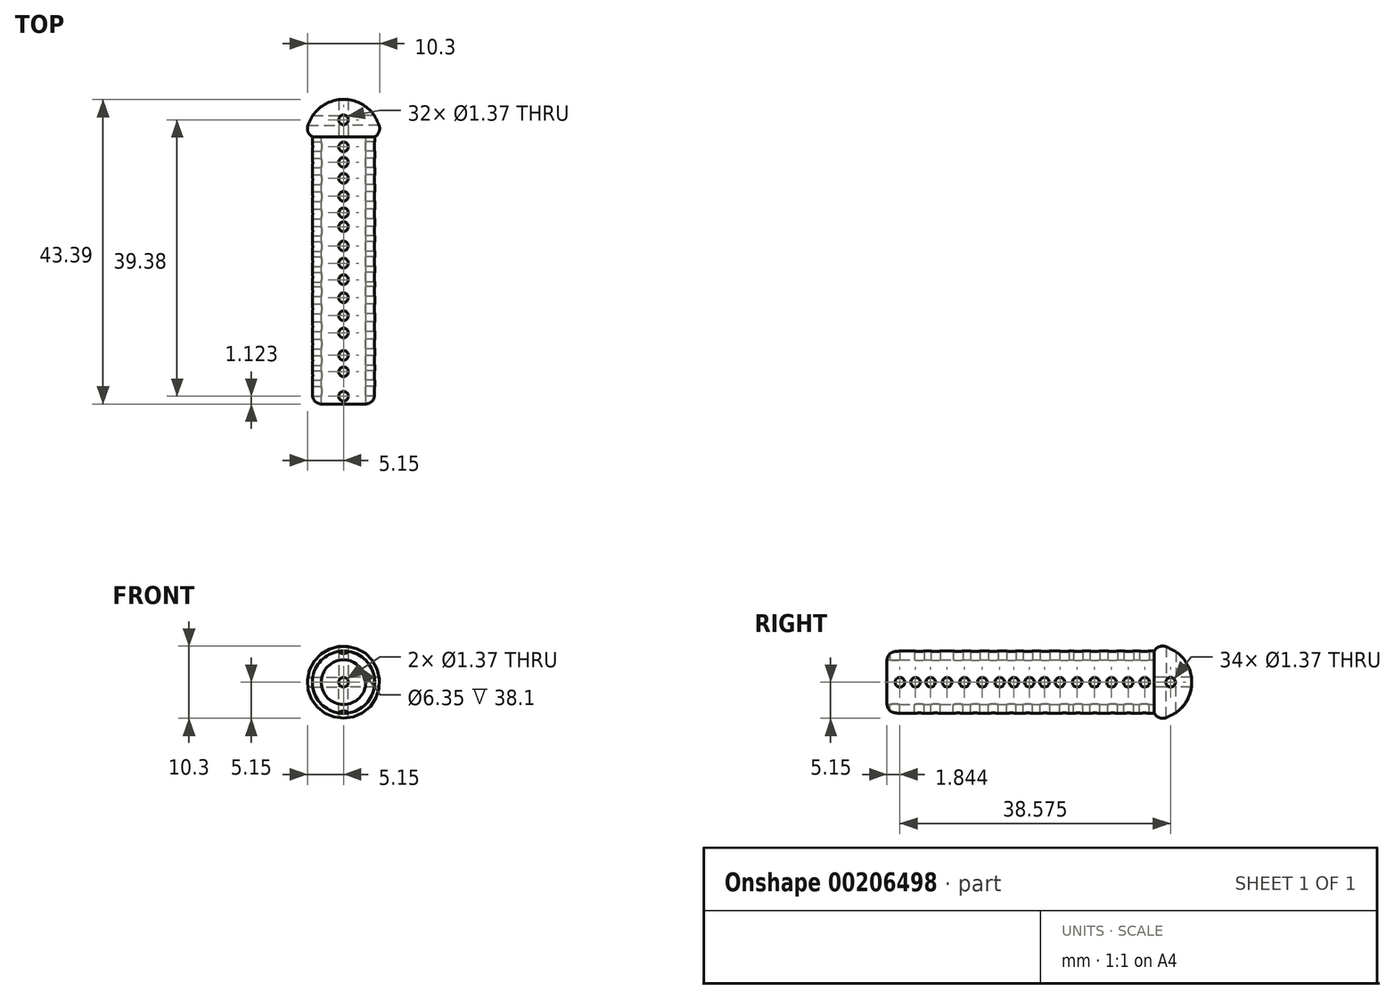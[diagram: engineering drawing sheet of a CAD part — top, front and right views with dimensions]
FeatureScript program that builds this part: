
annotation { "Feature Type Name" : "Feature", "Feature Type Description" : "" }
export const myFeature = defineFeature(function(context is Context, id is Id, definition is map)
    precondition{}
    {
        {
            var Q0;
            Q0=qCreatedBy(makeId("Front.planeOp"),FACE);
            var sketch = newSketch(context, id + "F0", { "sketchPlane" : qUnion([Q0])});
            skCircle(sketch, "E0", {"center": v(0, 0) * mm, "radius": 4.45 * mm});
            skCircle(sketch, "E1", {"center": v(0, 0) * mm, "radius": 3.18 * mm});
            skSolve(sketch);
        }
        {
            var Q0;
            Q0 = qSketchRegion(id + "F0", true);
            extrude(context, id + "F1", {"entities" : qUnion([Q0]), "depth" : 38.1 * mm});
        }
        {
            var Q0;
            Q0=qCreatedBy(makeId("Top.planeOp"),FACE);
            var sketch = newSketch(context, id + "F2", { "sketchPlane" : qUnion([Q0])});
            skArc(sketch, "E2", {"start": v(5.33, 0) * mm, "mid": v(3.77, 3.77) * mm, "end": v(0, 5.33) * mm});
            skLineSegment(sketch, "E3", {"start": v(0, 5.33) * mm, "end": v(0, 0) * mm});
            skLineSegment(sketch, "E4", {"start": v(5.33, 0) * mm, "end": v(0, 0) * mm});
            skSolve(sketch);
        }
        {
            var Q0;
            Q0 = qSketchRegion(id + "F2", true);
            var Q1;
            Q1=sQuery(id+"F2.wireOp",EDGE,"E3");
            revolve(context, id + "F3", {"operationType" : NewBodyOperationType.ADD, "entities" : qUnion([Q0]), "axis" : qUnion([Q1]), "revolveType" : RevolveType.FULL});
        }
        {
            var Q0;
            Q0 = qSketchRegion(id + "F0", true);
            extrude(context, id + "F4", {"entities" : qUnion([Q0]), "operationType" : NewBodyOperationType.ADD, "depth" : 38.1 * mm});
        }
        {
            var Q0;
            Q0=qCreatedBy(makeId("Right.planeOp"),FACE);
            var sketch = newSketch(context, id + "F5", { "sketchPlane" : qUnion([Q0])});
            skCircle(sketch, "E5", {"center": v(-1.37, 0) * mm, "radius": 0.64 * mm});
            skSolve(sketch);
        }
        {
            var Q0;
            Q0=sQuery(id+"F5.wireOp",VERTEX,"E5.center");
            var Q1;
            Q1=makeQuery(id+"F1.opExtrude","SWEPT_BODY",BODY,{"disambiguationData":[OSD([sQuery(id+"F0.wireOp",EDGE,"E0"),sQuery(id+"F0.wireOp",EDGE,"E1")])]});
            hole(context, id + "F6", {"style" : HoleStyle.SIMPLE, "endStyle" : HoleEndStyle.THROUGH, "holeDiameter" : 1.37 * mm, "locations" : qUnion([Q0]), "scope" : qUnion([Q1]), "isTappedThrough" : true});
        }
        {
            var Q0;
            Q0=qCreatedBy(makeId("Right.planeOp"),FACE);
            var sketch = newSketch(context, id + "F7", { "sketchPlane" : qUnion([Q0])});
            skCircle(sketch, "E6", {"center": v(-3.72, 0) * mm, "radius": 0.69 * mm});
            skSolve(sketch);
        }
        {
            var Q0;
            Q0=sQuery(id+"F5.wireOp",VERTEX,"E5.center");
            var Q1;
            Q1=makeQuery(id+"F1.opExtrude","SWEPT_BODY",BODY,{"disambiguationData":[OSD([sQuery(id+"F0.wireOp",EDGE,"E0"),sQuery(id+"F0.wireOp",EDGE,"E1")])]});
            hole(context, id + "F8", {"style" : HoleStyle.SIMPLE, "endStyle" : HoleEndStyle.THROUGH, "oppositeDirection" : true, "holeDiameter" : 1.37 * mm, "locations" : qUnion([Q0]), "scope" : qUnion([Q1]), "isTappedThrough" : true});
        }
        {
            var Q0;
            Q0=qCreatedBy(makeId("Right.planeOp"),FACE);
            var sketch = newSketch(context, id + "F9", { "sketchPlane" : qUnion([Q0])});
            skCircle(sketch, "E7", {"center": v(-6.1, 0) * mm, "radius": 0.69 * mm});
            skSolve(sketch);
        }
        {
            var Q0;
            Q0=sQuery(id+"F9.wireOp",VERTEX,"E7.center");
            var Q1;
            Q1=makeQuery(id+"F1.opExtrude","SWEPT_BODY",BODY,{"disambiguationData":[OSD([sQuery(id+"F0.wireOp",EDGE,"E0"),sQuery(id+"F0.wireOp",EDGE,"E1")])]});
            hole(context, id + "F10", {"style" : HoleStyle.SIMPLE, "endStyle" : HoleEndStyle.THROUGH, "holeDiameter" : 1.37 * mm, "locations" : qUnion([Q0]), "scope" : qUnion([Q1]), "isTappedThrough" : true});
        }
        {
            var Q0;
            Q0=sQuery(id+"F9.wireOp",VERTEX,"E7.center");
            var Q1;
            Q1=makeQuery(id+"F1.opExtrude","SWEPT_BODY",BODY,{"disambiguationData":[OSD([sQuery(id+"F0.wireOp",EDGE,"E0"),sQuery(id+"F0.wireOp",EDGE,"E1")])]});
            hole(context, id + "F11", {"style" : HoleStyle.SIMPLE, "endStyle" : HoleEndStyle.THROUGH, "oppositeDirection" : true, "holeDiameter" : 1.37 * mm, "locations" : qUnion([Q0]), "scope" : qUnion([Q1]), "isTappedThrough" : true});
        }
        {
            var Q0;
            Q0=sQuery(id+"F7.wireOp",VERTEX,"E6.center");
            var Q1;
            Q1=makeQuery(id+"F1.opExtrude","SWEPT_BODY",BODY,{"disambiguationData":[OSD([sQuery(id+"F0.wireOp",EDGE,"E0"),sQuery(id+"F0.wireOp",EDGE,"E1")])]});
            hole(context, id + "F12", {"style" : HoleStyle.SIMPLE, "endStyle" : HoleEndStyle.THROUGH, "holeDiameter" : 1.37 * mm, "locations" : qUnion([Q0]), "scope" : qUnion([Q1]), "isTappedThrough" : true});
        }
        {
            var Q0;
            Q0=sQuery(id+"F7.wireOp",VERTEX,"E6.center");
            var Q1;
            Q1=makeQuery(id+"F1.opExtrude","SWEPT_BODY",BODY,{"disambiguationData":[OSD([sQuery(id+"F0.wireOp",EDGE,"E0"),sQuery(id+"F0.wireOp",EDGE,"E1")])]});
            hole(context, id + "F13", {"style" : HoleStyle.SIMPLE, "endStyle" : HoleEndStyle.THROUGH, "oppositeDirection" : true, "holeDiameter" : 1.37 * mm, "locations" : qUnion([Q0]), "scope" : qUnion([Q1]), "isTappedThrough" : true});
        }
        {
            var Q0;
            Q0=qCreatedBy(makeId("Right.planeOp"),FACE);
            var sketch = newSketch(context, id + "F14", { "sketchPlane" : qUnion([Q0])});
            skCircle(sketch, "E8", {"center": v(-8.52, 0) * mm, "radius": 0.69 * mm});
            skSolve(sketch);
        }
        {
            var Q0;
            Q0=sQuery(id+"F14.wireOp",VERTEX,"E8.center");
            var Q1;
            Q1=makeQuery(id+"F1.opExtrude","SWEPT_BODY",BODY,{"disambiguationData":[OSD([sQuery(id+"F0.wireOp",EDGE,"E0"),sQuery(id+"F0.wireOp",EDGE,"E1")])]});
            hole(context, id + "F15", {"style" : HoleStyle.SIMPLE, "endStyle" : HoleEndStyle.THROUGH, "holeDiameter" : 1.37 * mm, "locations" : qUnion([Q0]), "scope" : qUnion([Q1]), "isTappedThrough" : true});
        }
        {
            var Q0;
            Q0=sQuery(id+"F14.wireOp",VERTEX,"E8.center");
            var Q1;
            Q1=makeQuery(id+"F1.opExtrude","SWEPT_BODY",BODY,{"disambiguationData":[OSD([sQuery(id+"F0.wireOp",EDGE,"E0"),sQuery(id+"F0.wireOp",EDGE,"E1")])]});
            hole(context, id + "F16", {"style" : HoleStyle.SIMPLE, "endStyle" : HoleEndStyle.THROUGH, "oppositeDirection" : true, "holeDiameter" : 1.37 * mm, "locations" : qUnion([Q0]), "scope" : qUnion([Q1]), "isTappedThrough" : true});
        }
        {
            var Q0;
            Q0=qCreatedBy(makeId("Right.planeOp"),FACE);
            var sketch = newSketch(context, id + "F17", { "sketchPlane" : qUnion([Q0])});
            skCircle(sketch, "E9", {"center": v(-11, 0) * mm, "radius": 0.69 * mm});
            skSolve(sketch);
        }
        {
            var Q0;
            Q0=sQuery(id+"F17.wireOp",VERTEX,"E9.center");
            var Q1;
            Q1=makeQuery(id+"F1.opExtrude","SWEPT_BODY",BODY,{"disambiguationData":[OSD([sQuery(id+"F0.wireOp",EDGE,"E0"),sQuery(id+"F0.wireOp",EDGE,"E1")])]});
            hole(context, id + "F18", {"style" : HoleStyle.SIMPLE, "endStyle" : HoleEndStyle.THROUGH, "holeDiameter" : 1.37 * mm, "locations" : qUnion([Q0]), "scope" : qUnion([Q1]), "isTappedThrough" : true});
        }
        {
            var Q0;
            Q0=sQuery(id+"F17.wireOp",VERTEX,"E9.center");
            var Q1;
            Q1=makeQuery(id+"F1.opExtrude","SWEPT_BODY",BODY,{"disambiguationData":[OSD([sQuery(id+"F0.wireOp",EDGE,"E0"),sQuery(id+"F0.wireOp",EDGE,"E1")])]});
            hole(context, id + "F19", {"style" : HoleStyle.SIMPLE, "endStyle" : HoleEndStyle.THROUGH, "oppositeDirection" : true, "holeDiameter" : 1.37 * mm, "locations" : qUnion([Q0]), "scope" : qUnion([Q1]), "isTappedThrough" : true});
        }
        {
            var Q0;
            Q0=qCreatedBy(makeId("Right.planeOp"),FACE);
            var sketch = newSketch(context, id + "F20", { "sketchPlane" : qUnion([Q0])});
            skCircle(sketch, "E10", {"center": v(-13.45, 0) * mm, "radius": 0.68 * mm});
            skSolve(sketch);
        }
        {
            var Q0;
            Q0=sQuery(id+"F20.wireOp",VERTEX,"E10.center");
            var Q1;
            Q1=makeQuery(id+"F1.opExtrude","SWEPT_BODY",BODY,{"disambiguationData":[OSD([sQuery(id+"F0.wireOp",EDGE,"E0"),sQuery(id+"F0.wireOp",EDGE,"E1")])]});
            hole(context, id + "F21", {"style" : HoleStyle.SIMPLE, "endStyle" : HoleEndStyle.THROUGH, "holeDiameter" : 1.37 * mm, "locations" : qUnion([Q0]), "scope" : qUnion([Q1]), "isTappedThrough" : true});
        }
        {
            var Q0;
            Q0=sQuery(id+"F20.wireOp",VERTEX,"E10.center");
            var Q1;
            Q1=makeQuery(id+"F1.opExtrude","SWEPT_BODY",BODY,{"disambiguationData":[OSD([sQuery(id+"F0.wireOp",EDGE,"E0"),sQuery(id+"F0.wireOp",EDGE,"E1")])]});
            hole(context, id + "F22", {"style" : HoleStyle.SIMPLE, "endStyle" : HoleEndStyle.THROUGH, "oppositeDirection" : true, "holeDiameter" : 1.37 * mm, "locations" : qUnion([Q0]), "scope" : qUnion([Q1]), "isTappedThrough" : true});
        }
        {
            var Q0;
            Q0=qCreatedBy(makeId("Right.planeOp"),FACE);
            var sketch = newSketch(context, id + "F23", { "sketchPlane" : qUnion([Q0])});
            skCircle(sketch, "E11", {"center": v(-15.65, 0) * mm, "radius": 0.69 * mm});
            skSolve(sketch);
        }
        {
            var Q0;
            Q0=sQuery(id+"F23.wireOp",VERTEX,"E11.center");
            var Q1;
            Q1=makeQuery(id+"F1.opExtrude","SWEPT_BODY",BODY,{"disambiguationData":[OSD([sQuery(id+"F0.wireOp",EDGE,"E0"),sQuery(id+"F0.wireOp",EDGE,"E1")])]});
            hole(context, id + "F24", {"style" : HoleStyle.SIMPLE, "endStyle" : HoleEndStyle.THROUGH, "holeDiameter" : 1.37 * mm, "locations" : qUnion([Q0]), "scope" : qUnion([Q1]), "isTappedThrough" : true});
        }
        {
            var Q0;
            Q0=sQuery(id+"F23.wireOp",VERTEX,"E11.center");
            var Q1;
            Q1=makeQuery(id+"F1.opExtrude","SWEPT_BODY",BODY,{"disambiguationData":[OSD([sQuery(id+"F0.wireOp",EDGE,"E0"),sQuery(id+"F0.wireOp",EDGE,"E1")])]});
            hole(context, id + "F25", {"style" : HoleStyle.SIMPLE, "endStyle" : HoleEndStyle.THROUGH, "oppositeDirection" : true, "holeDiameter" : 1.37 * mm, "locations" : qUnion([Q0]), "scope" : qUnion([Q1]), "isTappedThrough" : true});
        }
        {
            var Q0;
            Q0=qCreatedBy(makeId("Right.planeOp"),FACE);
            var sketch = newSketch(context, id + "F26", { "sketchPlane" : qUnion([Q0])});
            skCircle(sketch, "E12", {"center": v(-17.8, 0) * mm, "radius": 0.69 * mm});
            skSolve(sketch);
        }
        {
            var Q0;
            Q0=sQuery(id+"F26.wireOp",VERTEX,"E12.center");
            var Q1;
            Q1=makeQuery(id+"F1.opExtrude","SWEPT_BODY",BODY,{"disambiguationData":[OSD([sQuery(id+"F0.wireOp",EDGE,"E0"),sQuery(id+"F0.wireOp",EDGE,"E1")])]});
            hole(context, id + "F27", {"style" : HoleStyle.SIMPLE, "endStyle" : HoleEndStyle.THROUGH, "holeDiameter" : 1.37 * mm, "locations" : qUnion([Q0]), "scope" : qUnion([Q1]), "isTappedThrough" : true});
        }
        {
            var Q0;
            Q0=sQuery(id+"F26.wireOp",VERTEX,"E12.center");
            var Q1;
            Q1=makeQuery(id+"F1.opExtrude","SWEPT_BODY",BODY,{"disambiguationData":[OSD([sQuery(id+"F0.wireOp",EDGE,"E0"),sQuery(id+"F0.wireOp",EDGE,"E1")])]});
            hole(context, id + "F28", {"style" : HoleStyle.SIMPLE, "endStyle" : HoleEndStyle.THROUGH, "oppositeDirection" : true, "holeDiameter" : 1.37 * mm, "locations" : qUnion([Q0]), "scope" : qUnion([Q1]), "isTappedThrough" : true});
        }
        {
            var Q0;
            Q0=qCreatedBy(makeId("Right.planeOp"),FACE);
            var sketch = newSketch(context, id + "F29", { "sketchPlane" : qUnion([Q0])});
            skCircle(sketch, "E13", {"center": v(-20, 0) * mm, "radius": 0.69 * mm});
            skSolve(sketch);
        }
        {
            var Q0;
            Q0=sQuery(id+"F29.wireOp",VERTEX,"E13.center");
            var Q1;
            Q1=makeQuery(id+"F1.opExtrude","SWEPT_BODY",BODY,{"disambiguationData":[OSD([sQuery(id+"F0.wireOp",EDGE,"E0"),sQuery(id+"F0.wireOp",EDGE,"E1")])]});
            hole(context, id + "F30", {"style" : HoleStyle.SIMPLE, "endStyle" : HoleEndStyle.THROUGH, "holeDiameter" : 1.37 * mm, "locations" : qUnion([Q0]), "scope" : qUnion([Q1]), "isTappedThrough" : true});
        }
        {
            var Q0;
            Q0=sQuery(id+"F29.wireOp",VERTEX,"E13.center");
            var Q1;
            Q1=makeQuery(id+"F1.opExtrude","SWEPT_BODY",BODY,{"disambiguationData":[OSD([sQuery(id+"F0.wireOp",EDGE,"E0"),sQuery(id+"F0.wireOp",EDGE,"E1")])]});
            hole(context, id + "F31", {"style" : HoleStyle.SIMPLE, "endStyle" : HoleEndStyle.THROUGH, "oppositeDirection" : true, "holeDiameter" : 1.37 * mm, "locations" : qUnion([Q0]), "scope" : qUnion([Q1]), "isTappedThrough" : true});
        }
        {
            var Q0;
            Q0=qCreatedBy(makeId("Right.planeOp"),FACE);
            var sketch = newSketch(context, id + "F32", { "sketchPlane" : qUnion([Q0])});
            skCircle(sketch, "E14", {"center": v(-22.04, 0) * mm, "radius": 0.65 * mm});
            skSolve(sketch);
        }
        {
            var Q0;
            Q0=sQuery(id+"F32.wireOp",VERTEX,"E14.center");
            var Q1;
            Q1=makeQuery(id+"F1.opExtrude","SWEPT_BODY",BODY,{"disambiguationData":[OSD([sQuery(id+"F0.wireOp",EDGE,"E0"),sQuery(id+"F0.wireOp",EDGE,"E1")])]});
            hole(context, id + "F33", {"style" : HoleStyle.SIMPLE, "endStyle" : HoleEndStyle.THROUGH, "holeDiameter" : 1.37 * mm, "locations" : qUnion([Q0]), "scope" : qUnion([Q1]), "isTappedThrough" : true});
        }
        {
            var Q0;
            Q0=sQuery(id+"F32.wireOp",VERTEX,"E14.center");
            var Q1;
            Q1=makeQuery(id+"F1.opExtrude","SWEPT_BODY",BODY,{"disambiguationData":[OSD([sQuery(id+"F0.wireOp",EDGE,"E0"),sQuery(id+"F0.wireOp",EDGE,"E1")])]});
            hole(context, id + "F34", {"style" : HoleStyle.SIMPLE, "endStyle" : HoleEndStyle.THROUGH, "oppositeDirection" : true, "holeDiameter" : 1.37 * mm, "locations" : qUnion([Q0]), "scope" : qUnion([Q1]), "isTappedThrough" : true});
        }
        {
            var Q0;
            Q0=qCreatedBy(makeId("Right.planeOp"),FACE);
            var sketch = newSketch(context, id + "F35", { "sketchPlane" : qUnion([Q0])});
            skCircle(sketch, "E15", {"center": v(-24.51, 0) * mm, "radius": 0.7 * mm});
            skSolve(sketch);
        }
        {
            var Q0;
            Q0=sQuery(id+"F35.wireOp",VERTEX,"E15.center");
            var Q1;
            Q1=makeQuery(id+"F1.opExtrude","SWEPT_BODY",BODY,{"disambiguationData":[OSD([sQuery(id+"F0.wireOp",EDGE,"E0"),sQuery(id+"F0.wireOp",EDGE,"E1")])]});
            hole(context, id + "F36", {"style" : HoleStyle.SIMPLE, "endStyle" : HoleEndStyle.THROUGH, "holeDiameter" : 1.37 * mm, "locations" : qUnion([Q0]), "scope" : qUnion([Q1]), "isTappedThrough" : true});
        }
        {
            var Q0;
            Q0=sQuery(id+"F35.wireOp",VERTEX,"E15.center");
            var Q1;
            Q1=makeQuery(id+"F1.opExtrude","SWEPT_BODY",BODY,{"disambiguationData":[OSD([sQuery(id+"F0.wireOp",EDGE,"E0"),sQuery(id+"F0.wireOp",EDGE,"E1")])]});
            hole(context, id + "F37", {"style" : HoleStyle.SIMPLE, "endStyle" : HoleEndStyle.THROUGH, "oppositeDirection" : true, "holeDiameter" : 1.37 * mm, "locations" : qUnion([Q0]), "scope" : qUnion([Q1]), "isTappedThrough" : true});
        }
        {
            var Q0;
            Q0=qCreatedBy(makeId("Right.planeOp"),FACE);
            var sketch = newSketch(context, id + "F38", { "sketchPlane" : qUnion([Q0])});
            skCircle(sketch, "E16", {"center": v(-27.06, 0) * mm, "radius": 0.7 * mm});
            skSolve(sketch);
        }
        {
            var Q0;
            Q0=sQuery(id+"F38.wireOp",VERTEX,"E16.center");
            var Q1;
            Q1=makeQuery(id+"F1.opExtrude","SWEPT_BODY",BODY,{"disambiguationData":[OSD([sQuery(id+"F0.wireOp",EDGE,"E0"),sQuery(id+"F0.wireOp",EDGE,"E1")])]});
            hole(context, id + "F39", {"style" : HoleStyle.SIMPLE, "endStyle" : HoleEndStyle.THROUGH, "holeDiameter" : 1.37 * mm, "locations" : qUnion([Q0]), "scope" : qUnion([Q1]), "isTappedThrough" : true});
        }
        {
            var Q0;
            Q0=sQuery(id+"F38.wireOp",VERTEX,"E16.center");
            var Q1;
            Q1=makeQuery(id+"F1.opExtrude","SWEPT_BODY",BODY,{"disambiguationData":[OSD([sQuery(id+"F0.wireOp",EDGE,"E0"),sQuery(id+"F0.wireOp",EDGE,"E1")])]});
            hole(context, id + "F40", {"style" : HoleStyle.SIMPLE, "endStyle" : HoleEndStyle.THROUGH, "oppositeDirection" : true, "holeDiameter" : 1.37 * mm, "locations" : qUnion([Q0]), "scope" : qUnion([Q1]), "isTappedThrough" : true});
        }
        {
            var Q0;
            Q0=qCreatedBy(makeId("Right.planeOp"),FACE);
            var sketch = newSketch(context, id + "F41", { "sketchPlane" : qUnion([Q0])});
            skCircle(sketch, "E17", {"center": v(-29.53, 0) * mm, "radius": 0.69 * mm});
            skSolve(sketch);
        }
        {
            var Q0;
            Q0=sQuery(id+"F41.wireOp",VERTEX,"E17.center");
            var Q1;
            Q1=makeQuery(id+"F1.opExtrude","SWEPT_BODY",BODY,{"disambiguationData":[OSD([sQuery(id+"F0.wireOp",EDGE,"E0"),sQuery(id+"F0.wireOp",EDGE,"E1")])]});
            hole(context, id + "F42", {"style" : HoleStyle.SIMPLE, "endStyle" : HoleEndStyle.THROUGH, "holeDiameter" : 1.37 * mm, "locations" : qUnion([Q0]), "scope" : qUnion([Q1]), "isTappedThrough" : true});
        }
        {
            var Q0;
            Q0=sQuery(id+"F41.wireOp",VERTEX,"E17.center");
            var Q1;
            Q1=makeQuery(id+"F1.opExtrude","SWEPT_BODY",BODY,{"disambiguationData":[OSD([sQuery(id+"F0.wireOp",EDGE,"E0"),sQuery(id+"F0.wireOp",EDGE,"E1")])]});
            hole(context, id + "F43", {"style" : HoleStyle.SIMPLE, "endStyle" : HoleEndStyle.THROUGH, "oppositeDirection" : true, "holeDiameter" : 1.37 * mm, "locations" : qUnion([Q0]), "scope" : qUnion([Q1]), "isTappedThrough" : true});
        }
        {
            var Q0;
            Q0=qCreatedBy(makeId("Right.planeOp"),FACE);
            var sketch = newSketch(context, id + "F44", { "sketchPlane" : qUnion([Q0])});
            skCircle(sketch, "E18", {"center": v(-31.88, 0) * mm, "radius": 0.69 * mm});
            skSolve(sketch);
        }
        {
            var Q0;
            Q0=sQuery(id+"F44.wireOp",VERTEX,"E18.center");
            var Q1;
            Q1=makeQuery(id+"F1.opExtrude","SWEPT_BODY",BODY,{"disambiguationData":[OSD([sQuery(id+"F0.wireOp",EDGE,"E0"),sQuery(id+"F0.wireOp",EDGE,"E1")])]});
            hole(context, id + "F45", {"style" : HoleStyle.SIMPLE, "endStyle" : HoleEndStyle.THROUGH, "holeDiameter" : 1.37 * mm, "locations" : qUnion([Q0]), "scope" : qUnion([Q1]), "isTappedThrough" : true});
        }
        {
            var Q0;
            Q0=sQuery(id+"F44.wireOp",VERTEX,"E18.center");
            var Q1;
            Q1=makeQuery(id+"F1.opExtrude","SWEPT_BODY",BODY,{"disambiguationData":[OSD([sQuery(id+"F0.wireOp",EDGE,"E0"),sQuery(id+"F0.wireOp",EDGE,"E1")])]});
            hole(context, id + "F46", {"style" : HoleStyle.SIMPLE, "endStyle" : HoleEndStyle.THROUGH, "oppositeDirection" : true, "holeDiameter" : 1.37 * mm, "locations" : qUnion([Q0]), "scope" : qUnion([Q1]), "isTappedThrough" : true});
        }
        {
            var Q0;
            Q0=qCreatedBy(makeId("Right.planeOp"),FACE);
            var sketch = newSketch(context, id + "F47", { "sketchPlane" : qUnion([Q0])});
            skCircle(sketch, "E19", {"center": v(-34.03, 0) * mm, "radius": 0.69 * mm});
            skSolve(sketch);
        }
        {
            var Q0;
            Q0=sQuery(id+"F47.wireOp",VERTEX,"E19.center");
            var Q1;
            Q1=makeQuery(id+"F1.opExtrude","SWEPT_BODY",BODY,{"disambiguationData":[OSD([sQuery(id+"F0.wireOp",EDGE,"E0"),sQuery(id+"F0.wireOp",EDGE,"E1")])]});
            hole(context, id + "F48", {"style" : HoleStyle.SIMPLE, "endStyle" : HoleEndStyle.THROUGH, "holeDiameter" : 1.37 * mm, "locations" : qUnion([Q0]), "scope" : qUnion([Q1]), "isTappedThrough" : true});
        }
        {
            var Q0;
            Q0=sQuery(id+"F47.wireOp",VERTEX,"E19.center");
            var Q1;
            Q1=makeQuery(id+"F1.opExtrude","SWEPT_BODY",BODY,{"disambiguationData":[OSD([sQuery(id+"F0.wireOp",EDGE,"E0"),sQuery(id+"F0.wireOp",EDGE,"E1")])]});
            hole(context, id + "F49", {"style" : HoleStyle.SIMPLE, "endStyle" : HoleEndStyle.THROUGH, "oppositeDirection" : true, "holeDiameter" : 1.37 * mm, "locations" : qUnion([Q0]), "scope" : qUnion([Q1]), "isTappedThrough" : true});
        }
        {
            var Q0;
            Q0=qCreatedBy(makeId("Right.planeOp"),FACE);
            var sketch = newSketch(context, id + "F50", { "sketchPlane" : qUnion([Q0])});
            skCircle(sketch, "E20", {"center": v(-36.26, 0) * mm, "radius": 0.69 * mm});
            skSolve(sketch);
        }
        {
            var Q0;
            Q0=sQuery(id+"F50.wireOp",VERTEX,"E20.center");
            var Q1;
            Q1=makeQuery(id+"F1.opExtrude","SWEPT_BODY",BODY,{"disambiguationData":[OSD([sQuery(id+"F0.wireOp",EDGE,"E0"),sQuery(id+"F0.wireOp",EDGE,"E1")])]});
            hole(context, id + "F51", {"style" : HoleStyle.SIMPLE, "endStyle" : HoleEndStyle.THROUGH, "holeDiameter" : 1.37 * mm, "locations" : qUnion([Q0]), "scope" : qUnion([Q1]), "isTappedThrough" : true});
        }
        {
            var Q0;
            Q0=sQuery(id+"F50.wireOp",VERTEX,"E20.center");
            var Q1;
            Q1=makeQuery(id+"F1.opExtrude","SWEPT_BODY",BODY,{"disambiguationData":[OSD([sQuery(id+"F0.wireOp",EDGE,"E0"),sQuery(id+"F0.wireOp",EDGE,"E1")])]});
            hole(context, id + "F52", {"style" : HoleStyle.SIMPLE, "endStyle" : HoleEndStyle.THROUGH, "oppositeDirection" : true, "holeDiameter" : 1.37 * mm, "locations" : qUnion([Q0]), "scope" : qUnion([Q1]), "isTappedThrough" : true});
        }
        {
            var Q0;
            Q0=qCreatedBy(makeId("Front.planeOp"),FACE);
            var sketch = newSketch(context, id + "F53", { "sketchPlane" : qUnion([Q0])});
            skCircle(sketch, "E21", {"center": v(0, 0) * mm, "radius": 0.69 * mm});
            skSolve(sketch);
        }
        {
            var Q0;
            Q0=sQuery(id+"F53.wireOp",VERTEX,"E21.center");
            var Q1;
            Q1=makeQuery(id+"F1.opExtrude","SWEPT_BODY",BODY,{"disambiguationData":[OSD([sQuery(id+"F0.wireOp",EDGE,"E0"),sQuery(id+"F0.wireOp",EDGE,"E1")])]});
            hole(context, id + "F54", {"style" : HoleStyle.SIMPLE, "endStyle" : HoleEndStyle.THROUGH, "holeDiameter" : 1.37 * mm, "locations" : qUnion([Q0]), "scope" : qUnion([Q1]), "isTappedThrough" : true});
        }
        {
            var Q0;
            Q0=qCreatedBy(makeId("Right.planeOp"),FACE);
            var sketch = newSketch(context, id + "F55", { "sketchPlane" : qUnion([Q0])});
            skEllipse(sketch, "E22", {"center": v(2.32, 0) * mm, "majorRadius": 1.37 * mm, "minorRadius": 0.72 * mm, "majorAxis": v(1, 0)});
            skSolve(sketch);
        }
        {
            var Q0;
            Q0=sQuery(id+"F55.wireOp",VERTEX,"E22.center");
            var Q1;
            Q1=makeQuery(id+"F1.opExtrude","SWEPT_BODY",BODY,{"disambiguationData":[OSD([sQuery(id+"F0.wireOp",EDGE,"E0"),sQuery(id+"F0.wireOp",EDGE,"E1")])]});
            hole(context, id + "F56", {"style" : HoleStyle.SIMPLE, "endStyle" : HoleEndStyle.THROUGH, "holeDiameter" : 1.37 * mm, "locations" : qUnion([Q0]), "scope" : qUnion([Q1]), "isTappedThrough" : true});
        }
        {
            var Q0;
            Q0=sQuery(id+"F55.wireOp",VERTEX,"E22.center");
            var Q1;
            Q1=makeQuery(id+"F1.opExtrude","SWEPT_BODY",BODY,{"disambiguationData":[OSD([sQuery(id+"F0.wireOp",EDGE,"E0"),sQuery(id+"F0.wireOp",EDGE,"E1")])]});
            hole(context, id + "F57", {"style" : HoleStyle.SIMPLE, "endStyle" : HoleEndStyle.THROUGH, "oppositeDirection" : true, "holeDiameter" : 1.37 * mm, "locations" : qUnion([Q0]), "scope" : qUnion([Q1]), "isTappedThrough" : true});
        }
        {
            var Q0;
            Q0=qCreatedBy(makeId("Top.planeOp"),FACE);
            var sketch = newSketch(context, id + "F58", { "sketchPlane" : qUnion([Q0])});
            skCircle(sketch, "E23", {"center": v(0, -1.43) * mm, "radius": 0.69 * mm});
            skSolve(sketch);
        }
        {
            var Q0;
            Q0=sQuery(id+"F58.wireOp",VERTEX,"E23.center");
            var Q1;
            Q1=makeQuery(id+"F1.opExtrude","SWEPT_BODY",BODY,{"disambiguationData":[OSD([sQuery(id+"F0.wireOp",EDGE,"E0"),sQuery(id+"F0.wireOp",EDGE,"E1")])]});
            hole(context, id + "F59", {"style" : HoleStyle.SIMPLE, "endStyle" : HoleEndStyle.THROUGH, "holeDiameter" : 1.37 * mm, "locations" : qUnion([Q0]), "scope" : qUnion([Q1]), "isTappedThrough" : true});
        }
        {
            var Q0;
            Q0=sQuery(id+"F58.wireOp",VERTEX,"E23.center");
            var Q1;
            Q1=makeQuery(id+"F1.opExtrude","SWEPT_BODY",BODY,{"disambiguationData":[OSD([sQuery(id+"F0.wireOp",EDGE,"E0"),sQuery(id+"F0.wireOp",EDGE,"E1")])]});
            hole(context, id + "F60", {"style" : HoleStyle.SIMPLE, "endStyle" : HoleEndStyle.THROUGH, "oppositeDirection" : true, "holeDiameter" : 1.37 * mm, "locations" : qUnion([Q0]), "scope" : qUnion([Q1]), "isTappedThrough" : true});
        }
        {
            var Q0;
            Q0=qCreatedBy(makeId("Top.planeOp"),FACE);
            var sketch = newSketch(context, id + "F61", { "sketchPlane" : qUnion([Q0])});
            skCircle(sketch, "E24", {"center": v(0, -3.63) * mm, "radius": 0.69 * mm});
            skSolve(sketch);
        }
        {
            var Q0;
            Q0=sQuery(id+"F61.wireOp",VERTEX,"E24.center");
            var Q1;
            Q1=makeQuery(id+"F1.opExtrude","SWEPT_BODY",BODY,{"disambiguationData":[OSD([sQuery(id+"F0.wireOp",EDGE,"E0"),sQuery(id+"F0.wireOp",EDGE,"E1")])]});
            hole(context, id + "F62", {"style" : HoleStyle.SIMPLE, "endStyle" : HoleEndStyle.THROUGH, "holeDiameter" : 1.37 * mm, "locations" : qUnion([Q0]), "scope" : qUnion([Q1]), "isTappedThrough" : true});
        }
        {
            var Q0;
            Q0=sQuery(id+"F61.wireOp",VERTEX,"E24.center");
            var Q1;
            Q1=makeQuery(id+"F1.opExtrude","SWEPT_BODY",BODY,{"disambiguationData":[OSD([sQuery(id+"F0.wireOp",EDGE,"E0"),sQuery(id+"F0.wireOp",EDGE,"E1")])]});
            hole(context, id + "F63", {"style" : HoleStyle.SIMPLE, "endStyle" : HoleEndStyle.THROUGH, "oppositeDirection" : true, "holeDiameter" : 1.37 * mm, "locations" : qUnion([Q0]), "scope" : qUnion([Q1]), "isTappedThrough" : true});
        }
        {
            var Q0;
            Q0=qCreatedBy(makeId("Top.planeOp"),FACE);
            var sketch = newSketch(context, id + "F64", { "sketchPlane" : qUnion([Q0])});
            skCircle(sketch, "E25", {"center": v(0, -5.93) * mm, "radius": 0.69 * mm});
            skSolve(sketch);
        }
        {
            var Q0;
            Q0=sQuery(id+"F64.wireOp",VERTEX,"E25.center");
            var Q1;
            Q1=makeQuery(id+"F1.opExtrude","SWEPT_BODY",BODY,{"disambiguationData":[OSD([sQuery(id+"F0.wireOp",EDGE,"E0"),sQuery(id+"F0.wireOp",EDGE,"E1")])]});
            hole(context, id + "F65", {"style" : HoleStyle.SIMPLE, "endStyle" : HoleEndStyle.THROUGH, "holeDiameter" : 1.37 * mm, "locations" : qUnion([Q0]), "scope" : qUnion([Q1]), "isTappedThrough" : true});
        }
        {
            var Q0;
            Q0=sQuery(id+"F64.wireOp",VERTEX,"E25.center");
            var Q1;
            Q1=makeQuery(id+"F1.opExtrude","SWEPT_BODY",BODY,{"disambiguationData":[OSD([sQuery(id+"F0.wireOp",EDGE,"E0"),sQuery(id+"F0.wireOp",EDGE,"E1")])]});
            hole(context, id + "F66", {"style" : HoleStyle.SIMPLE, "endStyle" : HoleEndStyle.THROUGH, "oppositeDirection" : true, "holeDiameter" : 1.37 * mm, "locations" : qUnion([Q0]), "scope" : qUnion([Q1]), "isTappedThrough" : true});
        }
        {
            var Q0;
            Q0=qCreatedBy(makeId("Top.planeOp"),FACE);
            var sketch = newSketch(context, id + "F67", { "sketchPlane" : qUnion([Q0])});
            skCircle(sketch, "E26", {"center": v(0, -8.48) * mm, "radius": 0.7 * mm});
            skSolve(sketch);
        }
        {
            var Q0;
            Q0=sQuery(id+"F67.wireOp",VERTEX,"E26.center");
            var Q1;
            Q1=makeQuery(id+"F1.opExtrude","SWEPT_BODY",BODY,{"disambiguationData":[OSD([sQuery(id+"F0.wireOp",EDGE,"E0"),sQuery(id+"F0.wireOp",EDGE,"E1")])]});
            hole(context, id + "F68", {"style" : HoleStyle.SIMPLE, "endStyle" : HoleEndStyle.THROUGH, "holeDiameter" : 1.37 * mm, "locations" : qUnion([Q0]), "scope" : qUnion([Q1]), "isTappedThrough" : true});
        }
        {
            var Q0;
            Q0=sQuery(id+"F67.wireOp",VERTEX,"E26.center");
            var Q1;
            Q1=makeQuery(id+"F1.opExtrude","SWEPT_BODY",BODY,{"disambiguationData":[OSD([sQuery(id+"F0.wireOp",EDGE,"E0"),sQuery(id+"F0.wireOp",EDGE,"E1")])]});
            hole(context, id + "F69", {"style" : HoleStyle.SIMPLE, "endStyle" : HoleEndStyle.THROUGH, "oppositeDirection" : true, "holeDiameter" : 1.37 * mm, "locations" : qUnion([Q0]), "scope" : qUnion([Q1]), "isTappedThrough" : true});
        }
        {
            var Q0;
            Q0=qCreatedBy(makeId("Top.planeOp"),FACE);
            var sketch = newSketch(context, id + "F70", { "sketchPlane" : qUnion([Q0])});
            skCircle(sketch, "E27", {"center": v(0, -10.84) * mm, "radius": 0.7 * mm});
            skSolve(sketch);
        }
        {
            var Q0;
            Q0=sQuery(id+"F70.wireOp",VERTEX,"E27.center");
            var Q1;
            Q1=makeQuery(id+"F1.opExtrude","SWEPT_BODY",BODY,{"disambiguationData":[OSD([sQuery(id+"F0.wireOp",EDGE,"E0"),sQuery(id+"F0.wireOp",EDGE,"E1")])]});
            hole(context, id + "F71", {"style" : HoleStyle.SIMPLE, "endStyle" : HoleEndStyle.THROUGH, "holeDiameter" : 1.37 * mm, "locations" : qUnion([Q0]), "scope" : qUnion([Q1]), "isTappedThrough" : true});
        }
        {
            var Q0;
            Q0=sQuery(id+"F70.wireOp",VERTEX,"E27.center");
            var Q1;
            Q1=makeQuery(id+"F1.opExtrude","SWEPT_BODY",BODY,{"disambiguationData":[OSD([sQuery(id+"F0.wireOp",EDGE,"E0"),sQuery(id+"F0.wireOp",EDGE,"E1")])]});
            hole(context, id + "F72", {"style" : HoleStyle.SIMPLE, "endStyle" : HoleEndStyle.THROUGH, "oppositeDirection" : true, "holeDiameter" : 1.37 * mm, "locations" : qUnion([Q0]), "scope" : qUnion([Q1]), "isTappedThrough" : true});
        }
        {
            var Q0;
            Q0=qCreatedBy(makeId("Top.planeOp"),FACE);
            var sketch = newSketch(context, id + "F73", { "sketchPlane" : qUnion([Q0])});
            skCircle(sketch, "E28", {"center": v(0, -12.81) * mm, "radius": 0.69 * mm});
            skSolve(sketch);
        }
        {
            var Q0;
            Q0=sQuery(id+"F73.wireOp",VERTEX,"E28.center");
            var Q1;
            Q1=makeQuery(id+"F1.opExtrude","SWEPT_BODY",BODY,{"disambiguationData":[OSD([sQuery(id+"F0.wireOp",EDGE,"E0"),sQuery(id+"F0.wireOp",EDGE,"E1")])]});
            hole(context, id + "F74", {"style" : HoleStyle.SIMPLE, "endStyle" : HoleEndStyle.THROUGH, "holeDiameter" : 1.37 * mm, "locations" : qUnion([Q0]), "scope" : qUnion([Q1]), "isTappedThrough" : true});
        }
        {
            var Q0;
            Q0=sQuery(id+"F73.wireOp",VERTEX,"E28.center");
            var Q1;
            Q1=makeQuery(id+"F1.opExtrude","SWEPT_BODY",BODY,{"disambiguationData":[OSD([sQuery(id+"F0.wireOp",EDGE,"E0"),sQuery(id+"F0.wireOp",EDGE,"E1")])]});
            hole(context, id + "F75", {"style" : HoleStyle.SIMPLE, "endStyle" : HoleEndStyle.THROUGH, "oppositeDirection" : true, "holeDiameter" : 1.37 * mm, "locations" : qUnion([Q0]), "scope" : qUnion([Q1]), "isTappedThrough" : true});
        }
        {
            var Q0;
            Q0=qCreatedBy(makeId("Top.planeOp"),FACE);
            var sketch = newSketch(context, id + "F76", { "sketchPlane" : qUnion([Q0])});
            skCircle(sketch, "E29", {"center": v(0, -15.57) * mm, "radius": 0.69 * mm});
            skSolve(sketch);
        }
        {
            var Q0;
            Q0=sQuery(id+"F76.wireOp",VERTEX,"E29.center");
            var Q1;
            Q1=makeQuery(id+"F1.opExtrude","SWEPT_BODY",BODY,{"disambiguationData":[OSD([sQuery(id+"F0.wireOp",EDGE,"E0"),sQuery(id+"F0.wireOp",EDGE,"E1")])]});
            hole(context, id + "F77", {"style" : HoleStyle.SIMPLE, "endStyle" : HoleEndStyle.THROUGH, "holeDiameter" : 1.37 * mm, "locations" : qUnion([Q0]), "scope" : qUnion([Q1]), "isTappedThrough" : true});
        }
        {
            var Q0;
            Q0=sQuery(id+"F76.wireOp",VERTEX,"E29.center");
            var Q1;
            Q1=makeQuery(id+"F1.opExtrude","SWEPT_BODY",BODY,{"disambiguationData":[OSD([sQuery(id+"F0.wireOp",EDGE,"E0"),sQuery(id+"F0.wireOp",EDGE,"E1")])]});
            hole(context, id + "F78", {"style" : HoleStyle.SIMPLE, "endStyle" : HoleEndStyle.THROUGH, "oppositeDirection" : true, "holeDiameter" : 1.37 * mm, "locations" : qUnion([Q0]), "scope" : qUnion([Q1]), "isTappedThrough" : true});
        }
        {
            var Q0;
            Q0=qCreatedBy(makeId("Top.planeOp"),FACE);
            var sketch = newSketch(context, id + "F79", { "sketchPlane" : qUnion([Q0])});
            skCircle(sketch, "E30", {"center": v(0, -18.02) * mm, "radius": 0.68 * mm});
            skSolve(sketch);
        }
        {
            var Q0;
            Q0=sQuery(id+"F79.wireOp",VERTEX,"E30.center");
            var Q1;
            Q1=makeQuery(id+"F1.opExtrude","SWEPT_BODY",BODY,{"disambiguationData":[OSD([sQuery(id+"F0.wireOp",EDGE,"E0"),sQuery(id+"F0.wireOp",EDGE,"E1")])]});
            hole(context, id + "F80", {"style" : HoleStyle.SIMPLE, "endStyle" : HoleEndStyle.THROUGH, "holeDiameter" : 1.37 * mm, "locations" : qUnion([Q0]), "scope" : qUnion([Q1]), "isTappedThrough" : true});
        }
        {
            var Q0;
            Q0=sQuery(id+"F79.wireOp",VERTEX,"E30.center");
            var Q1;
            Q1=makeQuery(id+"F1.opExtrude","SWEPT_BODY",BODY,{"disambiguationData":[OSD([sQuery(id+"F0.wireOp",EDGE,"E0"),sQuery(id+"F0.wireOp",EDGE,"E1")])]});
            hole(context, id + "F81", {"style" : HoleStyle.SIMPLE, "endStyle" : HoleEndStyle.THROUGH, "oppositeDirection" : true, "holeDiameter" : 1.37 * mm, "locations" : qUnion([Q0]), "scope" : qUnion([Q1]), "isTappedThrough" : true});
        }
        {
            var Q0;
            Q0=qCreatedBy(makeId("Top.planeOp"),FACE);
            var sketch = newSketch(context, id + "F82", { "sketchPlane" : qUnion([Q0])});
            skCircle(sketch, "E31", {"center": v(0, -20.37) * mm, "radius": 0.69 * mm});
            skSolve(sketch);
        }
        {
            var Q0;
            Q0=sQuery(id+"F82.wireOp",VERTEX,"E31.center");
            var Q1;
            Q1=makeQuery(id+"F1.opExtrude","SWEPT_BODY",BODY,{"disambiguationData":[OSD([sQuery(id+"F0.wireOp",EDGE,"E0"),sQuery(id+"F0.wireOp",EDGE,"E1")])]});
            hole(context, id + "F83", {"style" : HoleStyle.SIMPLE, "endStyle" : HoleEndStyle.THROUGH, "holeDiameter" : 1.37 * mm, "locations" : qUnion([Q0]), "scope" : qUnion([Q1]), "isTappedThrough" : true});
        }
        {
            var Q0;
            Q0=sQuery(id+"F82.wireOp",VERTEX,"E31.center");
            var Q1;
            Q1=makeQuery(id+"F1.opExtrude","SWEPT_BODY",BODY,{"disambiguationData":[OSD([sQuery(id+"F0.wireOp",EDGE,"E0"),sQuery(id+"F0.wireOp",EDGE,"E1")])]});
            hole(context, id + "F84", {"style" : HoleStyle.SIMPLE, "endStyle" : HoleEndStyle.THROUGH, "oppositeDirection" : true, "holeDiameter" : 1.37 * mm, "locations" : qUnion([Q0]), "scope" : qUnion([Q1]), "isTappedThrough" : true});
        }
        {
            var Q0;
            Q0=qCreatedBy(makeId("Top.planeOp"),FACE);
            var sketch = newSketch(context, id + "F85", { "sketchPlane" : qUnion([Q0])});
            skCircle(sketch, "E32", {"center": v(0, -25.5) * mm, "radius": 0.69 * mm});
            skSolve(sketch);
        }
        {
            var Q0;
            Q0=sQuery(id+"F85.wireOp",VERTEX,"E32.center");
            var Q1;
            Q1=makeQuery(id+"F1.opExtrude","SWEPT_BODY",BODY,{"disambiguationData":[OSD([sQuery(id+"F0.wireOp",EDGE,"E0"),sQuery(id+"F0.wireOp",EDGE,"E1")])]});
            hole(context, id + "F86", {"style" : HoleStyle.SIMPLE, "endStyle" : HoleEndStyle.THROUGH, "holeDiameter" : 1.37 * mm, "locations" : qUnion([Q0]), "scope" : qUnion([Q1]), "isTappedThrough" : true});
        }
        {
            var Q0;
            Q0=sQuery(id+"F85.wireOp",VERTEX,"E32.center");
            var Q1;
            Q1=makeQuery(id+"F1.opExtrude","SWEPT_BODY",BODY,{"disambiguationData":[OSD([sQuery(id+"F0.wireOp",EDGE,"E0"),sQuery(id+"F0.wireOp",EDGE,"E1")])]});
            hole(context, id + "F87", {"style" : HoleStyle.SIMPLE, "endStyle" : HoleEndStyle.THROUGH, "oppositeDirection" : true, "holeDiameter" : 1.37 * mm, "locations" : qUnion([Q0]), "scope" : qUnion([Q1]), "isTappedThrough" : true});
        }
        {
            var Q0;
            Q0=qCreatedBy(makeId("Top.planeOp"),FACE);
            var sketch = newSketch(context, id + "F88", { "sketchPlane" : qUnion([Q0])});
            skCircle(sketch, "E33", {"center": v(0, -22.94) * mm, "radius": 0.69 * mm});
            skSolve(sketch);
        }
        {
            var Q0;
            Q0=sQuery(id+"F88.wireOp",VERTEX,"E33.center");
            var Q1;
            Q1=makeQuery(id+"F1.opExtrude","SWEPT_BODY",BODY,{"disambiguationData":[OSD([sQuery(id+"F0.wireOp",EDGE,"E0"),sQuery(id+"F0.wireOp",EDGE,"E1")])]});
            hole(context, id + "F89", {"style" : HoleStyle.SIMPLE, "endStyle" : HoleEndStyle.THROUGH, "holeDiameter" : 1.37 * mm, "locations" : qUnion([Q0]), "scope" : qUnion([Q1]), "isTappedThrough" : true});
        }
        {
            var Q0;
            Q0=sQuery(id+"F88.wireOp",VERTEX,"E33.center");
            var Q1;
            Q1=makeQuery(id+"F1.opExtrude","SWEPT_BODY",BODY,{"disambiguationData":[OSD([sQuery(id+"F0.wireOp",EDGE,"E0"),sQuery(id+"F0.wireOp",EDGE,"E1")])]});
            hole(context, id + "F90", {"style" : HoleStyle.SIMPLE, "endStyle" : HoleEndStyle.THROUGH, "oppositeDirection" : true, "holeDiameter" : 1.37 * mm, "locations" : qUnion([Q0]), "scope" : qUnion([Q1]), "isTappedThrough" : true});
        }
        {
            var Q0;
            Q0=qCreatedBy(makeId("Top.planeOp"),FACE);
            var sketch = newSketch(context, id + "F91", { "sketchPlane" : qUnion([Q0])});
            skCircle(sketch, "E34", {"center": v(0, -27.96) * mm, "radius": 0.68 * mm});
            skSolve(sketch);
        }
        {
            var Q0;
            Q0=sQuery(id+"F91.wireOp",VERTEX,"E34.center");
            var Q1;
            Q1=makeQuery(id+"F1.opExtrude","SWEPT_BODY",BODY,{"disambiguationData":[OSD([sQuery(id+"F0.wireOp",EDGE,"E0"),sQuery(id+"F0.wireOp",EDGE,"E1")])]});
            hole(context, id + "F92", {"style" : HoleStyle.SIMPLE, "endStyle" : HoleEndStyle.THROUGH, "holeDiameter" : 1.37 * mm, "locations" : qUnion([Q0]), "scope" : qUnion([Q1]), "isTappedThrough" : true});
        }
        {
            var Q0;
            Q0=sQuery(id+"F91.wireOp",VERTEX,"E34.center");
            var Q1;
            Q1=makeQuery(id+"F1.opExtrude","SWEPT_BODY",BODY,{"disambiguationData":[OSD([sQuery(id+"F0.wireOp",EDGE,"E0"),sQuery(id+"F0.wireOp",EDGE,"E1")])]});
            hole(context, id + "F93", {"style" : HoleStyle.SIMPLE, "endStyle" : HoleEndStyle.THROUGH, "oppositeDirection" : true, "holeDiameter" : 1.37 * mm, "locations" : qUnion([Q0]), "scope" : qUnion([Q1]), "isTappedThrough" : true});
        }
        {
            var Q0;
            Q0=qCreatedBy(makeId("Top.planeOp"),FACE);
            var sketch = newSketch(context, id + "F94", { "sketchPlane" : qUnion([Q0])});
            skCircle(sketch, "E35", {"center": v(0, -31.16) * mm, "radius": 0.69 * mm});
            skSolve(sketch);
        }
        {
            var Q0;
            Q0=sQuery(id+"F94.wireOp",VERTEX,"E35.center");
            var Q1;
            Q1=makeQuery(id+"F1.opExtrude","SWEPT_BODY",BODY,{"disambiguationData":[OSD([sQuery(id+"F0.wireOp",EDGE,"E0"),sQuery(id+"F0.wireOp",EDGE,"E1")])]});
            hole(context, id + "F95", {"style" : HoleStyle.SIMPLE, "endStyle" : HoleEndStyle.THROUGH, "holeDiameter" : 1.37 * mm, "locations" : qUnion([Q0]), "scope" : qUnion([Q1]), "isTappedThrough" : true});
        }
        {
            var Q0;
            Q0=sQuery(id+"F94.wireOp",VERTEX,"E35.center");
            var Q1;
            Q1=makeQuery(id+"F1.opExtrude","SWEPT_BODY",BODY,{"disambiguationData":[OSD([sQuery(id+"F0.wireOp",EDGE,"E0"),sQuery(id+"F0.wireOp",EDGE,"E1")])]});
            hole(context, id + "F96", {"style" : HoleStyle.SIMPLE, "endStyle" : HoleEndStyle.THROUGH, "oppositeDirection" : true, "holeDiameter" : 1.37 * mm, "locations" : qUnion([Q0]), "scope" : qUnion([Q1]), "isTappedThrough" : true});
        }
        {
            var Q0;
            Q0=qCreatedBy(makeId("Top.planeOp"),FACE);
            var sketch = newSketch(context, id + "F97", { "sketchPlane" : qUnion([Q0])});
            skCircle(sketch, "E36", {"center": v(0, -33.5) * mm, "radius": 0.68 * mm});
            skSolve(sketch);
        }
        {
            var Q0;
            Q0=sQuery(id+"F97.wireOp",VERTEX,"E36.center");
            var Q1;
            Q1=makeQuery(id+"F1.opExtrude","SWEPT_BODY",BODY,{"disambiguationData":[OSD([sQuery(id+"F0.wireOp",EDGE,"E0"),sQuery(id+"F0.wireOp",EDGE,"E1")])]});
            hole(context, id + "F98", {"style" : HoleStyle.SIMPLE, "endStyle" : HoleEndStyle.THROUGH, "holeDiameter" : 1.37 * mm, "locations" : qUnion([Q0]), "scope" : qUnion([Q1]), "isTappedThrough" : true});
        }
        {
            var Q0;
            Q0=sQuery(id+"F97.wireOp",VERTEX,"E36.center");
            var Q1;
            Q1=makeQuery(id+"F1.opExtrude","SWEPT_BODY",BODY,{"disambiguationData":[OSD([sQuery(id+"F0.wireOp",EDGE,"E0"),sQuery(id+"F0.wireOp",EDGE,"E1")])]});
            hole(context, id + "F99", {"style" : HoleStyle.SIMPLE, "endStyle" : HoleEndStyle.THROUGH, "oppositeDirection" : true, "holeDiameter" : 1.37 * mm, "locations" : qUnion([Q0]), "scope" : qUnion([Q1]), "isTappedThrough" : true});
        }
        {
            var Q0;
            Q0=qCreatedBy(makeId("Top.planeOp"),FACE);
            var sketch = newSketch(context, id + "F100", { "sketchPlane" : qUnion([Q0])});
            skCircle(sketch, "E37", {"center": v(0, -36.98) * mm, "radius": 0.68 * mm});
            skSolve(sketch);
        }
        {
            var Q0;
            Q0=sQuery(id+"F100.wireOp",VERTEX,"E37.center");
            var Q1;
            Q1=makeQuery(id+"F1.opExtrude","SWEPT_BODY",BODY,{"disambiguationData":[OSD([sQuery(id+"F0.wireOp",EDGE,"E0"),sQuery(id+"F0.wireOp",EDGE,"E1")])]});
            hole(context, id + "F101", {"style" : HoleStyle.SIMPLE, "endStyle" : HoleEndStyle.THROUGH, "holeDiameter" : 1.37 * mm, "locations" : qUnion([Q0]), "scope" : qUnion([Q1]), "isTappedThrough" : true});
        }
        {
            var Q0;
            Q0=sQuery(id+"F100.wireOp",VERTEX,"E37.center");
            var Q1;
            Q1=makeQuery(id+"F1.opExtrude","SWEPT_BODY",BODY,{"disambiguationData":[OSD([sQuery(id+"F0.wireOp",EDGE,"E0"),sQuery(id+"F0.wireOp",EDGE,"E1")])]});
            hole(context, id + "F102", {"style" : HoleStyle.SIMPLE, "endStyle" : HoleEndStyle.THROUGH, "oppositeDirection" : true, "holeDiameter" : 1.37 * mm, "locations" : qUnion([Q0]), "scope" : qUnion([Q1]), "isTappedThrough" : true});
        }
        {
            var Q0;
            Q0=qCreatedBy(makeId("Top.planeOp"),FACE);
            var sketch = newSketch(context, id + "F103", { "sketchPlane" : qUnion([Q0])});
            skCircle(sketch, "E38", {"center": v(0, 2.4) * mm, "radius": 0.69 * mm});
            skSolve(sketch);
        }
        {
            var Q0;
            Q0=sQuery(id+"F103.wireOp",VERTEX,"E38.center");
            var Q1;
            Q1=makeQuery(id+"F1.opExtrude","SWEPT_BODY",BODY,{"disambiguationData":[OSD([sQuery(id+"F0.wireOp",EDGE,"E0"),sQuery(id+"F0.wireOp",EDGE,"E1")])]});
            hole(context, id + "F104", {"style" : HoleStyle.SIMPLE, "endStyle" : HoleEndStyle.THROUGH, "holeDiameter" : 1.37 * mm, "locations" : qUnion([Q0]), "scope" : qUnion([Q1]), "isTappedThrough" : true});
        }
        {
            var Q0;
            Q0=sQuery(id+"F103.wireOp",VERTEX,"E38.center");
            var Q1;
            Q1=makeQuery(id+"F1.opExtrude","SWEPT_BODY",BODY,{"disambiguationData":[OSD([sQuery(id+"F0.wireOp",EDGE,"E0"),sQuery(id+"F0.wireOp",EDGE,"E1")])]});
            hole(context, id + "F105", {"style" : HoleStyle.SIMPLE, "endStyle" : HoleEndStyle.THROUGH, "oppositeDirection" : true, "holeDiameter" : 1.37 * mm, "locations" : qUnion([Q0]), "scope" : qUnion([Q1]), "isTappedThrough" : true});
        }
        {
            var Q0;
            Q0=makeQuery(id+"F3.opRevolve","SWEPT_EDGE",EDGE,{"disambiguationData":[OSD([sQuery(id+"F2.wireOp",EDGE,"E2"),sQuery(id+"F2.wireOp",EDGE,"E4")])]});
            fillet(context, id + "F106", {"entities" : qUnion([Q0]), "radius" : 1.37 * mm, "tangentPropagation" : true, "allowEdgeOverflow" : false});
        }
        {
            var Q0;
            Q0=makeQuery(id+"F1.opExtrude","CAP_EDGE",EDGE,{"disambiguationData":[OSD([sQuery(id+"F0.wireOp",EDGE,"E0")])],"isStart":false});
            fillet(context, id + "F107", {"entities" : qUnion([Q0]), "radius" : 1.37 * mm, "tangentPropagation" : true, "allowEdgeOverflow" : false});
        }
    });
